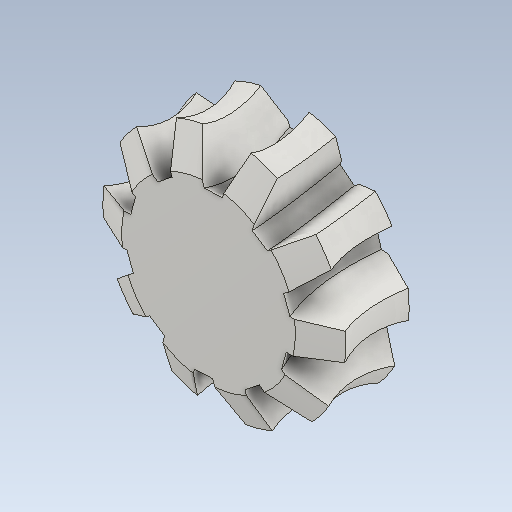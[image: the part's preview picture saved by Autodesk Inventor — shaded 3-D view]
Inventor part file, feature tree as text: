
AUTODESK INVENTOR PART (.ipt)
format: ipt  version: 2021 (Build 250183000, 183)  size: 313,344 bytes
history: native  units: mm (DEFAULTED — no unit token found)
features: other x8, plane x3, pattern_circular x1, sketch x1
ambient origin geometry x5: Origin, X Axis, Y Axis, Z Axis, Center Point
bodies: Solid1 (feature_tree)
feature tree (13):
  other  "Tooth Plane"
  other  "Base Body Sketch"
  other  "Base Body"
  other  "Base Body2"
  plane  "Work Plane13"
  other  "Tooth"
  pattern_circular  "Tooth Pattern"  [2 undecoded]
  plane  "Work Plane14"
  plane  "Work Plane15"
  other  "Tooth Sketch"
  sketch  "Sketch8"  dims[d35=90.0deg d37=-1.001674mm d38=40.117556mm d39=3.490659mm d40=14.8mm d41=20.0mm d42=3.788903mm d43=90.0deg d44=100.0mm d46=360.0deg d50=4.297754mm d68=40.117556mm d69=0.0mm d73=0.0mm d75=3.141593mm d77=40.201513mm d78=20.0mm d79=0.0mm d80=0.0mm d81=0.0mm d82=0.0mm d83=3.141593mm d84=0.0mm d85=180.0deg d86=40.117556mm d87=52.235113mm d89=32.0mm d90=90.0deg d92=20.0mm d93=40.117556mm]
  other  "Srf1"
  other  "Pitch Diameter"
note: 2 required parameter values undecoded (feature->parameter linkage not recoverable at this tier; creation-order binding heuristic only, values carry confidence <= 0.55)
